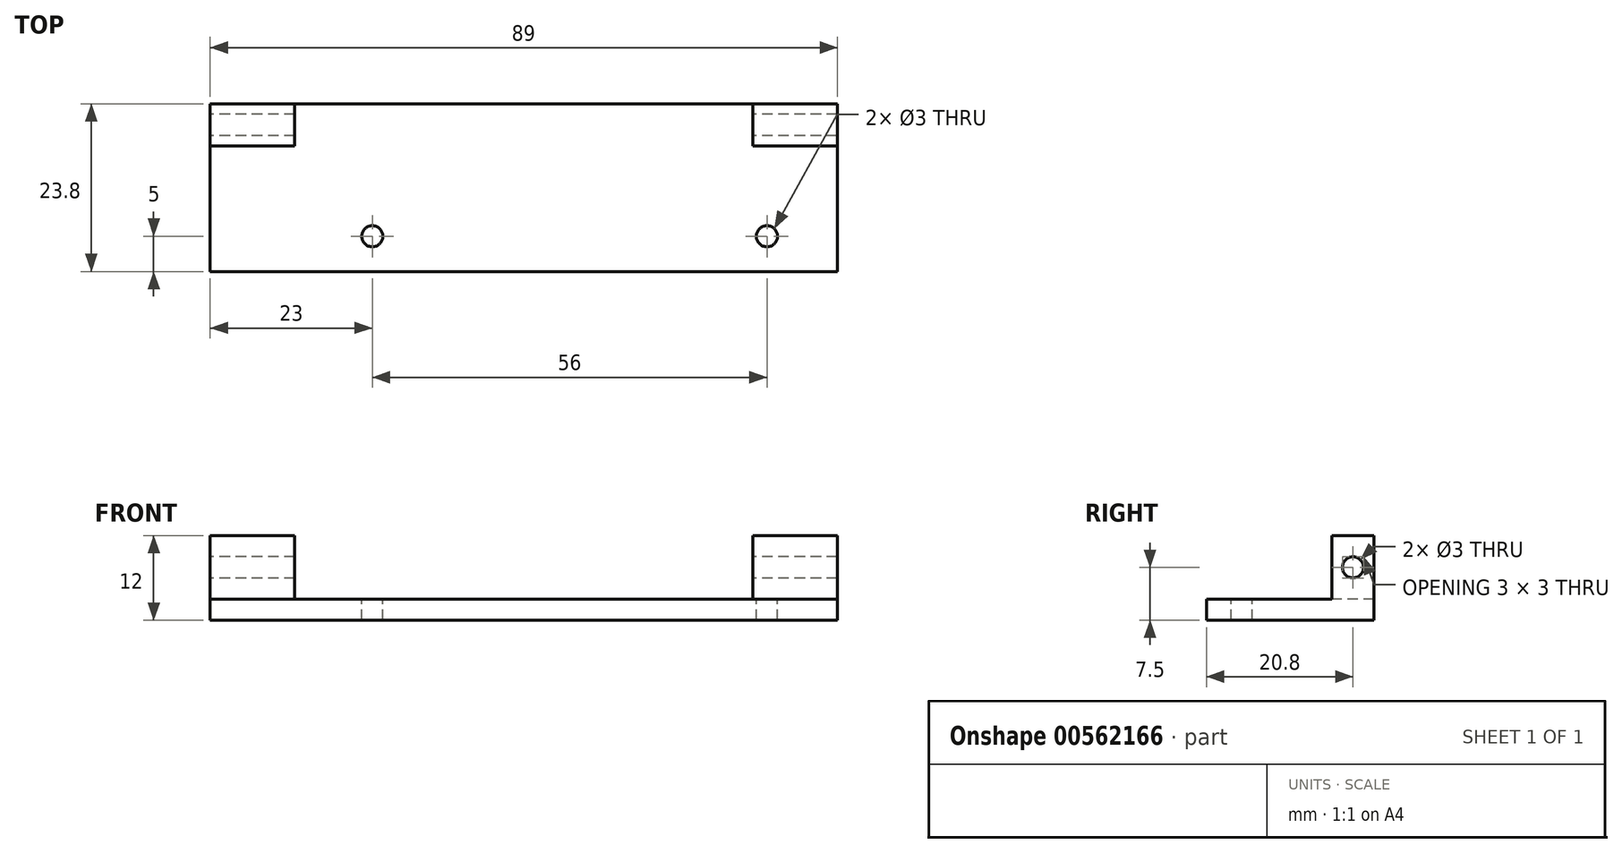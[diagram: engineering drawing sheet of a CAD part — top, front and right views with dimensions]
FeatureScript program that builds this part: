
annotation { "Feature Type Name" : "Feature", "Feature Type Description" : "" }
export const myFeature = defineFeature(function(context is Context, id is Id, definition is map)
    precondition{}
    {
        {
            var Q0;
            Q0=qCreatedBy(makeId("Top.planeOp"),FACE);
            var sketch = newSketch(context, id + "F0", { "sketchPlane" : qUnion([Q0])});
            skLineSegment(sketch, "E0.bottom", {"start": v(44.5, -11.9) * mm, "end": v(-44.5, -11.9) * mm});
            skLineSegment(sketch, "E0.top", {"start": v(44.5, 11.9) * mm, "end": v(-44.5, 11.9) * mm});
            skLineSegment(sketch, "E0.left", {"start": v(44.5, -11.9) * mm, "end": v(44.5, 11.9) * mm});
            skLineSegment(sketch, "E0.right", {"start": v(-44.5, -11.9) * mm, "end": v(-44.5, 11.9) * mm});
            skPoint(sketch, "E0.middle", {"position": v(0, 0) * mm});
            skSolve(sketch);
        }
        {
            var Q0;
            Q0=makeQuery(id+"F0.imprint","IMPRINT",FACE,{"disambiguationData":[TD([[makeQuery(id+"F0.imprint","IMPRINT",EDGE,{"derivedFrom":sQuery(id+"F0.wireOp",EDGE,"E0.bottom")}),-1.0]])]});
            extrude(context, id + "F1", {"entities" : qUnion([Q0]), "depth" : 3 * mm, "offsetDistance" : 25 * mm});
        }
        {
            var Q0;
            Q0=makeQuery(id+"F1.opExtrude","CAP_FACE",FACE,{"disambiguationData":[OSD([sQuery(id+"F0.wireOp",EDGE,"E0.bottom"),sQuery(id+"F0.wireOp",EDGE,"E0.top"),sQuery(id+"F0.wireOp",EDGE,"E0.left"),sQuery(id+"F0.wireOp",EDGE,"E0.right")])],"isStart":false});
            var sketch = newSketch(context, id + "F2", { "sketchPlane" : qUnion([Q0])});
            skLineSegment(sketch, "E1.bottom", {"start": v(44.5, 11.9) * mm, "end": v(32.5, 11.9) * mm});
            skLineSegment(sketch, "E1.top", {"start": v(44.5, 5.9) * mm, "end": v(32.5, 5.9) * mm});
            skLineSegment(sketch, "E1.left", {"start": v(44.5, 11.9) * mm, "end": v(44.5, 5.9) * mm});
            skLineSegment(sketch, "E1.right", {"start": v(32.5, 11.9) * mm, "end": v(32.5, 5.9) * mm});
            skSolve(sketch);
        }
        {
            var Q0;
            {var subQ4=sQuery(id+"F2.wireOp",EDGE,"E1.top");Q0=makeQuery(id+"F2.imprint","IMPRINT",FACE,{"disambiguationData":[TD([[makeQuery(id+"F2.imprint","IMPRINT",EDGE,{"derivedFrom":subQ4}),1.0]])]});}
            var sketch = newSketch(context, id + "F3", { "sketchPlane" : qUnion([Q0])});
            skLineSegment(sketch, "E2.bottom", {"start": v(-44.5, 11.9) * mm, "end": v(-32.5, 11.9) * mm});
            skLineSegment(sketch, "E2.top", {"start": v(-44.5, 5.9) * mm, "end": v(-32.5, 5.9) * mm});
            skLineSegment(sketch, "E2.left", {"start": v(-44.5, 11.9) * mm, "end": v(-44.5, 5.9) * mm});
            skLineSegment(sketch, "E2.right", {"start": v(-32.5, 11.9) * mm, "end": v(-32.5, 5.9) * mm});
            skSolve(sketch);
        }
        {
            var Q0;
            Q0=makeQuery(id+"F2.imprint","IMPRINT",FACE,{"disambiguationData":[TD([[makeQuery(id+"F2.imprint","IMPRINT",EDGE,{"derivedFrom":sQuery(id+"F2.wireOp",EDGE,"E1.bottom")}),1.0]])]});
            var Q1;
            Q1=makeQuery(id+"F3.imprint","IMPRINT",FACE,{"disambiguationData":[TD([[makeQuery(id+"F3.imprint","IMPRINT",EDGE,{"derivedFrom":sQuery(id+"F3.wireOp",EDGE,"E2.bottom")}),1.0]])]});
            extrude(context, id + "F4", {"entities" : qUnion([Q0, Q1]), "operationType" : NewBodyOperationType.ADD, "depth" : 9 * mm, "offsetDistance" : 25 * mm});
        }
        {
            var Q0;
            Q0=makeQuery(id+"F4.boolean.opBoolean","MERGE",FACE,{"derivedFrom":[makeQuery(id+"F1.opExtrude","SWEPT_FACE",FACE,{"disambiguationData":[OSD([sQuery(id+"F0.wireOp",EDGE,"E0.right")])]}),makeQuery(id+"F4.opExtrude","SWEPT_FACE",FACE,{"disambiguationData":[OSD([sQuery(id+"F3.wireOp",EDGE,"E2.left")])]})]});
            var sketch = newSketch(context, id + "F5", { "sketchPlane" : qUnion([Q0])});
            skCircle(sketch, "E3", {"center": v(-8.9, 7.5) * mm, "radius": 1.5 * mm});
            skSolve(sketch);
        }
        {
            var Q0;
            Q0=makeQuery(id+"F5.imprint","IMPRINT",FACE,{"disambiguationData":[TD([[makeQuery(id+"F5.imprint","IMPRINT",EDGE,{"derivedFrom":sQuery(id+"F5.wireOp",EDGE,"E3")}),1.0]])]});
            extrude(context, id + "F6", {"entities" : qUnion([Q0]), "operationType" : NewBodyOperationType.REMOVE, "endBound" : BoundingType.THROUGH_ALL, "oppositeDirection" : true, "depth" : 25 * mm, "offsetDistance" : 25 * mm});
        }
        {
            var Q0;
            Q0=makeQuery(id+"F1.opExtrude","CAP_FACE",FACE,{"disambiguationData":[OSD([sQuery(id+"F0.wireOp",EDGE,"E0.bottom"),sQuery(id+"F0.wireOp",EDGE,"E0.top"),sQuery(id+"F0.wireOp",EDGE,"E0.left"),sQuery(id+"F0.wireOp",EDGE,"E0.right")])],"isStart":false});
            var sketch = newSketch(context, id + "F7", { "sketchPlane" : qUnion([Q0])});
            skCircle(sketch, "E4", {"center": v(34.5, -6.9) * mm, "radius": 1.5 * mm});
            skSolve(sketch);
        }
        {
            var Q0;
            Q0=makeQuery(id+"F7.imprint","IMPRINT",FACE,{"disambiguationData":[TD([[makeQuery(id+"F7.imprint","IMPRINT",EDGE,{"derivedFrom":sQuery(id+"F7.wireOp",EDGE,"E4")}),-1.0]])]});
            var sketch = newSketch(context, id + "F8", { "sketchPlane" : qUnion([Q0])});
            skCircle(sketch, "E5", {"center": v(-21.5, -6.9) * mm, "radius": 1.5 * mm});
            skSolve(sketch);
        }
        {
            var Q0;
            Q0 = qSketchRegion(id + "F7", true);
            var Q1;
            Q1 = qSketchRegion(id + "F8", true);
            extrude(context, id + "F9", {"entities" : qUnion([Q0, Q1]), "operationType" : NewBodyOperationType.REMOVE, "oppositeDirection" : true, "depth" : 15 * mm, "offsetDistance" : 25 * mm});
        }
    });
